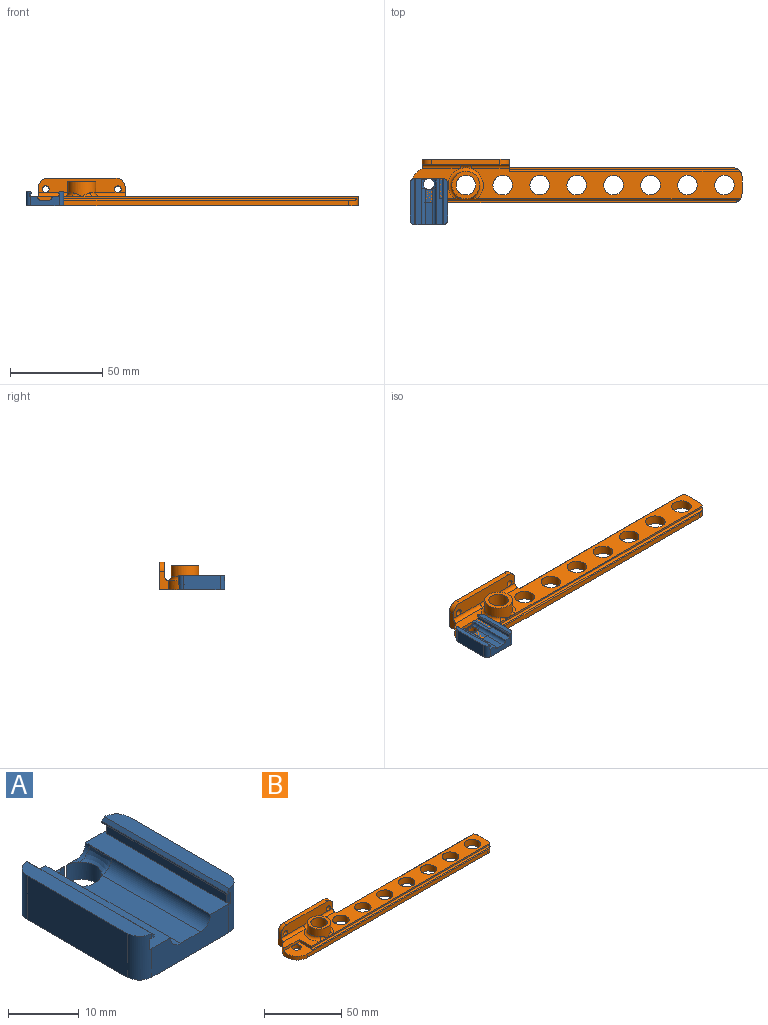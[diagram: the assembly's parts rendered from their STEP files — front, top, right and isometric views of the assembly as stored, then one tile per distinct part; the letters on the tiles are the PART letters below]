
ASSEMBLY  parts=2 mates=1
PART A: 46 faces, bbox 20.4x25x7.6 mm
  f0: plane 19.77x4mm, normal (0,0,1), area 77mm2, adj f2,f15,f42,f45
  f1: plane 1.81x0.76mm, normal (0,0,1), area 0.5mm2, adj f4,f15,f43
  f2: plane 15.4x5mm, normal (0,-1,0), area 62.7mm2, adj f0,f8,f16,f19,f25,f26,f42,f45
  f3: plane 0.72x0.45mm, normal (0,-1,0), area 0.2mm2, adj f22,f25,f30,f39
  f4: plane 7.51x5mm, normal (0,1,0), area 30.8mm2, adj f1,f8,f15,f16,f24,f43
  f5: plane 7.51x5mm, normal (0,1,0), area 30.8mm2, adj f9,f15,f16,f19,f27,f40
  f6: plane 24x1.6mm, normal (-1,0,0), area 38.4mm2, adj f19,f32,f34,f37
  f7: plane 24x1.6mm, normal (1,0,0), area 38.4mm2, adj f8,f29,f35,f36
  f8: plane 25x4.12mm, normal (0,0,1), area 91.5mm2, adj f2,f4,f7,f17,f24,f25,f35,f36
  f9: plane 1.81x0.76mm, normal (0,0,1), area 0.5mm2, adj f5,f15,f40
  f10: plane 0.72x0.45mm, normal (0,1,0), area 0.2mm2, adj f22,f24,f28,f39
  f11: plane 20x7.6mm, normal (-1,0,0), area 152mm2, adj f16,f20,f24,f25
  f12: plane 0.72x0.45mm, normal (0,-1,0), area 0.2mm2, adj f23,f26,f31,f38
  f13: plane 20x7.6mm, normal (1,0,0), area 152mm2, adj f16,f21,f26,f27
  f14: plane 0.72x0.45mm, normal (0,1,0), area 0.2mm2, adj f23,f27,f33,f38
  f15: cylinder r=3mm len=6mm, axis (0,0,-1), area 55.4mm2, adj f0,f1,f4,f5,f9,f16,f41,f44
  f16: plane 25x20.4mm, normal (0,0,-1), area 476.4mm2, adj f2,f4,f5,f11,f13,f15,f24,f25
  f17: plane 4.48x0.27mm, normal (1,0,0), area 0.6mm2, adj f8,f44
  f18: plane 4.47x0.27mm, normal (-1,0,0), area 0.6mm2, adj f19,f41
  f19: plane 25x4.12mm, normal (0,0,1), area 91.5mm2, adj f2,f5,f6,f18,f26,f27,f34,f37
  f20: plane 25x2.45mm, normal (0,0,1), area 58.6mm2, adj f11,f24,f25,f39
  f21: plane 25x2.45mm, normal (0,0,1), area 58.6mm2, adj f13,f26,f27,f38
  f22: plane 25x0.27mm, normal (1,0,0), area 6.7mm2, adj f3,f10,f29,f39
  f23: plane 25x0.27mm, normal (-1,0,0), area 6.7mm2, adj f12,f14,f32,f38
  f24: cylinder r=2.5mm len=7.6mm, axis (0,0,1), area 29.1mm2, adj f4,f8,f10,f11,f16,f20,f28,f35
  f25: cylinder r=2.5mm len=7.6mm, axis (0,0,1), area 29.1mm2, adj f2,f3,f8,f11,f16,f20,f30,f36
  f26: cylinder r=2.5mm len=7.6mm, axis (0,0,1), area 29.1mm2, adj f2,f12,f13,f16,f19,f21,f31,f37
  f27: cylinder r=2.5mm len=7.6mm, axis (0,0,1), area 29.1mm2, adj f5,f13,f14,f16,f19,f21,f33,f34
  f28: plane 0.88x0.46mm, normal (0,0.5,-0.87), area 0.2mm2, adj f10,f24,f29,f35
  f29: plane 25x0.45mm, normal (0.5,0,-0.87), area 11.4mm2, adj f7,f22,f28,f30,f35,f36
  f30: plane 0.88x0.46mm, normal (0,-0.5,-0.87), area 0.2mm2, adj f3,f25,f29,f36
  f31: plane 0.88x0.46mm, normal (0,-0.5,-0.87), area 0.2mm2, adj f12,f26,f32,f37
  f32: plane 25x0.45mm, normal (-0.5,0,-0.87), area 11.4mm2, adj f6,f23,f31,f33,f34,f37
  f33: plane 0.88x0.46mm, normal (0,0.5,-0.87), area 0.2mm2, adj f14,f27,f32,f34
  f34: plane 1.81x0.47mm, normal (-0.71,0.71,0), area 1.1mm2, adj f6,f19,f27,f32,f33
  f35: plane 1.81x0.47mm, normal (0.71,0.71,0), area 1.1mm2, adj f7,f8,f24,f28,f29
  f36: plane 1.81x0.47mm, normal (0.71,-0.71,0), area 1.1mm2, adj f7,f8,f25,f29,f30
  f37: plane 1.81x0.47mm, normal (-0.71,-0.71,0), area 1.1mm2, adj f6,f19,f26,f31,f32
  f38: plane 25x0.5mm, normal (-0.71,0,0.71), area 17.7mm2, adj f12,f14,f21,f23,f26,f27
  f39: plane 25x0.5mm, normal (0.71,0,0.71), area 17.7mm2, adj f3,f10,f20,f22,f24,f25
  f40: cylinder r=2mm len=2mm, axis (0,1,0), area 2.4mm2, adj f5,f9,f19,f41
  f41: bspline ~4.47x2mm, area 10.9mm2, adj f15,f18,f40,f42
  f42: cylinder r=2mm len=19.77mm, axis (0,1,0), area 62.1mm2, adj f0,f2,f19,f41
  f43: cylinder r=2mm len=2mm, axis (0,-1,0), area 2.4mm2, adj f1,f4,f8,f44
  f44: bspline ~4.47x2mm, area 10.9mm2, adj f15,f17,f43,f45
  f45: cylinder r=2mm len=19.77mm, axis (0,-1,0), area 62.1mm2, adj f0,f2,f8,f44
PART B: 43 faces, bbox 179.8x24.3x15.8 mm
  f0: plane 146.46x16.5mm, normal (0,0,1), area 1525.3mm2, adj f4,f5,f6,f8,f12,f13,f14,f15
  f1: plane 25.75x16.5mm, normal (0,0,1), area 172.6mm2, adj f10,f11,f23,f24,f26,f32,f38
  f2: plane 177x13.11mm, normal (0,0,1), area 309.2mm2, adj f3,f4,f11,f20,f23,f26,f30
  f3: plane 164.5x3mm, normal (0,-1,0), area 493.5mm2, adj f2,f4,f11,f22
  f4: cylinder r=5mm len=5mm, axis (0,0,-1), area 30.7mm2, adj f0,f2,f3,f5,f22,f24,f30
  f5: plane 9x5mm, normal (1,0,0), area 45mm2, adj f0,f4,f6,f22
  f6: cylinder r=5mm len=5mm, axis (0,0,-1), area 30.7mm2, adj f0,f5,f7,f21,f22,f25,f29
  f7: plane 121x3mm, normal (0,1,0), area 363mm2, adj f6,f8,f21,f22
  f8: plane 10x6.5mm, normal (1,0,0), area 42.1mm2, adj f0,f7,f9,f21,f22,f25,f29,f34
  f9: plane 47x15mm, normal (0,1,0), area 673.9mm2, adj f8,f10,f22,f35,f36,f37,f41,f42
  f10: plane 10x5.17mm, normal (-1,0,0), area 41.7mm2, adj f1,f9,f11,f22,f34,f38,f41
  f11: cylinder r=9.5mm len=18.33mm, axis (0,0,-1), area 94.1mm2, adj f1,f2,f3,f10,f22,f26
  f12: cylinder r=5.3mm len=10.6mm, axis (0,0,-1), area 166.5mm2, adj f0,f22
  f13: cylinder r=5.3mm len=10.6mm, axis (0,0,-1), area 166.5mm2, adj f0,f22
  f14: cylinder r=5.3mm len=10.6mm, axis (0,0,-1), area 166.5mm2, adj f0,f22
  f15: cylinder r=5.3mm len=10.6mm, axis (0,0,-1), area 166.5mm2, adj f0,f22
  f16: cylinder r=5.3mm len=10.6mm, axis (0,0,-1), area 166.5mm2, adj f0,f22
  f17: cylinder r=5.3mm len=10.6mm, axis (0,0,-1), area 166.5mm2, adj f0,f22
  f18: cylinder r=5.3mm len=10.6mm, axis (0,0,-1), area 166.5mm2, adj f0,f22
  f19: cylinder r=5.3mm len=13mm, axis (0,0,-1), area 432.9mm2, adj f22,f28
  f20: cylinder r=3mm len=6mm, axis (0,0,-1), area 56.5mm2, adj f2,f22
  f21: plane 124x1mm, normal (0,0,1), area 123mm2, adj f6,f7,f8,f29
  f22: plane 179x23.5mm, normal (0,0,-1), area 2829.5mm2, adj f3,f4,f5,f6,f7,f8,f9,f10
  f23: plane 12.11x2mm, normal (-1,0,0), area 22.4mm2, adj f1,f2,f24,f26,f30
  f24: plane 163.79x1.79mm, normal (0,-1,0), area 163mm2, adj f0,f1,f4,f23,f30,f31,f33
  f25: plane 125x1mm, normal (0,1,0), area 125mm2, adj f0,f6,f8,f29
  f26: plane 14.29x2mm, normal (0,-1,0), area 28.6mm2, adj f1,f2,f11,f23
  f27: cylinder r=7.5mm len=15mm, axis (0,0,-1), area 292.7mm2, adj f28,f31,f32,f33
  f28: plane 15x15mm, normal (0,0,1), area 88.5mm2, adj f19,f27
  f29: cylinder r=1mm len=125mm, axis (1,0,0), area 195.6mm2, adj f6,f8,f21,f25
  f30: cylinder r=1mm len=163mm, axis (-1,0,0), area 255.3mm2, adj f2,f4,f23,f24
  f31: bspline ~5.99x2.08mm, area 5mm2, adj f24,f27,f32
  f32: torus R=9.5mm, axis (0,0,1), area 128.2mm2, adj f0,f1,f27,f31,f33,f39
  f33: bspline ~6.44x2.43mm, area 5mm2, adj f24,f27,f32
  f34: plane 47x8.06mm, normal (0,-1,0), area 345.1mm2, adj f8,f10,f35,f36,f37,f38,f39,f40
  f35: plane 37x3mm, normal (0,0,1), area 111mm2, adj f9,f34,f41,f42
  f36: cylinder r=1.8mm len=3.6mm, axis (0,1,0), area 33.9mm2, adj f9,f34
  f37: cylinder r=1.8mm len=3.6mm, axis (0,1,0), area 33.9mm2, adj f9,f34
  f38: cylinder r=2mm len=20.46mm, axis (-1,0,0), area 64.3mm2, adj f1,f10,f34,f39
  f39: bspline ~7.93x2.46mm, area 17mm2, adj f32,f34,f38,f40
  f40: cylinder r=2mm len=20.46mm, axis (-1,0,0), area 64.3mm2, adj f0,f8,f34,f39
  f41: cylinder r=5mm len=5mm, axis (0,1,0), area 23.6mm2, adj f9,f10,f34,f35
  f42: cylinder r=5mm len=5mm, axis (0,-1,0), area 23.6mm2, adj f8,f9,f34,f35
PLACE A t=(-20,-11.94,0)mm
PLACE B at identity fixed
MATE fastened B.f20 <-> A.f15  axis (0,0,-1) through (-20,0.57,0)mm
